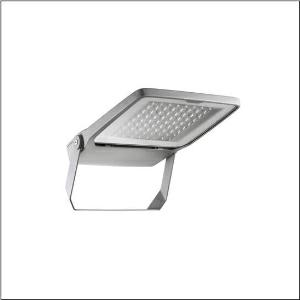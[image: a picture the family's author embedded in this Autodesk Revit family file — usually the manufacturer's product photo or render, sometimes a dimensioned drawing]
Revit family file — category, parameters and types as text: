
# Revit family: floodlight_fl_20_mini___rs17_5xa7671c2b1ac_996d
name_source: partatom
category: Lighting Fixtures
units: mm (PartAtom-declared; Revit-internal decimal feet)

## family parameters
Cut with Voids When Loaded = No
Host = Face
Light Source = No
Part Type = Normal
Room Calculation Point = No
Round Connector Dimension = Use Diameter
Shared = No

## types (1)
- Floodlight FL 20 mini  RS17 (1 x LED 4000K / CRI = 70 (unbekannt), 13350 lm, 4000K)
    Apparent Load = 96 VA
    CIE Flux Codes = 79 92 99 100 100
    Color Rendering = 70
    Color Temperature = 4000K
    Default Elevation = 1800 mm
    Description = Floodlight FL 20 mini, floodlight, primary light control with lens, of plastic, primary optical cover: protective disc, of toughened safety glass, transparent, light distribution: RS17, light emission: direct distribution, primary light characteristic: rotationally symmetric, installation type: surface-mounted, LED, High Power LED, rated luminous flux: 13.350lm, luminous efficacy: 139lm/W, light colour: 740, colour temperature: 4000K, control gear: ECG Basic, control: power reduction, overheat protection, electronic power reduction, with terminal, 5-pole, max. 2.5mm², mains connection: 220..240V, AC, 50/60Hz, rated input power: 96W, LED unit, of diecast aluminium, powder-coated, Siteco® metallic grey (DB 702S), corrosivity category C5 mid according to DIN EN ISO 12944, incl. 1x M20 cable gland for cable Ø 6.5..12mm, length: 446mm, width: 355mm, height: 62mm, housing frame, of diecast aluminium, powder-coated, Siteco® metallic grey (DB 702S), mounting bracket, of steel, powder-coated, Siteco® metallic grey (DB 702S), ON/OFF, protection rating (complete): IP66, insulation class (complete): insulation class I (protective earthing), certification: CE, ENEC, VDE, protection symbol: D, permissible operating ambient temperature: -40..+40°C, permissible operating ambient temperature for outdoor applications: -40..+50°C, standard: DIN EN 12944, packaging unit: 1 piece

Light Distribution: RS17
    Height = 62 mm  [stored 0.203412 ft]
    Lamp = 1 x LED 4000K / CRI >= 70 (unbekannt)
    Lamp Light Flux = 13350 lm
    Lamp count = 1
    Length = 467 mm
    Luminous efficacy = 139 lm/W
    Manufacturer = Siteco
    ModVariant = No
    Model = 5XA7671C2B1AC
    Mounting Place = Wall
    Mounting Type = Surface mounted
    Number of Poles = 1
    OnlyDefault = Yes
    Power Factor = 1
    Product Name = Floodlight FL 20 mini | RS17
    Product group = floodlight | wall mounted
    ProductGroupID = 2001
    Protection Class = Protection class I
    Protection Degree = IP 66
    RLX_Detail_Level = 1
    RLX_Emergency_Light_Flux = 0 lm
    RLX_Emergency_Type = 0
    RLX_Emergency_Type_DB = No
    RlxData = <blob elided: 65981 chars, md5=859478ad>
    Socket = socket
    Standby Power = 0 W
    System Light Flux = 13350 lm
    System Power = 96 W
    Type Comments = Product without accessories
    Type Image = l_1005948.jpg
    URL = http://relux.com
    VarID = ---
    Voltage = 0 V
    Weight = 0.00 kg
    Width = 335 mm

note: [stored X ft] marks values corroborated as IEEE doubles in the binary element streams (Revit-internal decimal feet)

## geometry (parser evidence)
native form markers: Blend x4, Sweep x12
no freeform markers — native parametric forms only
